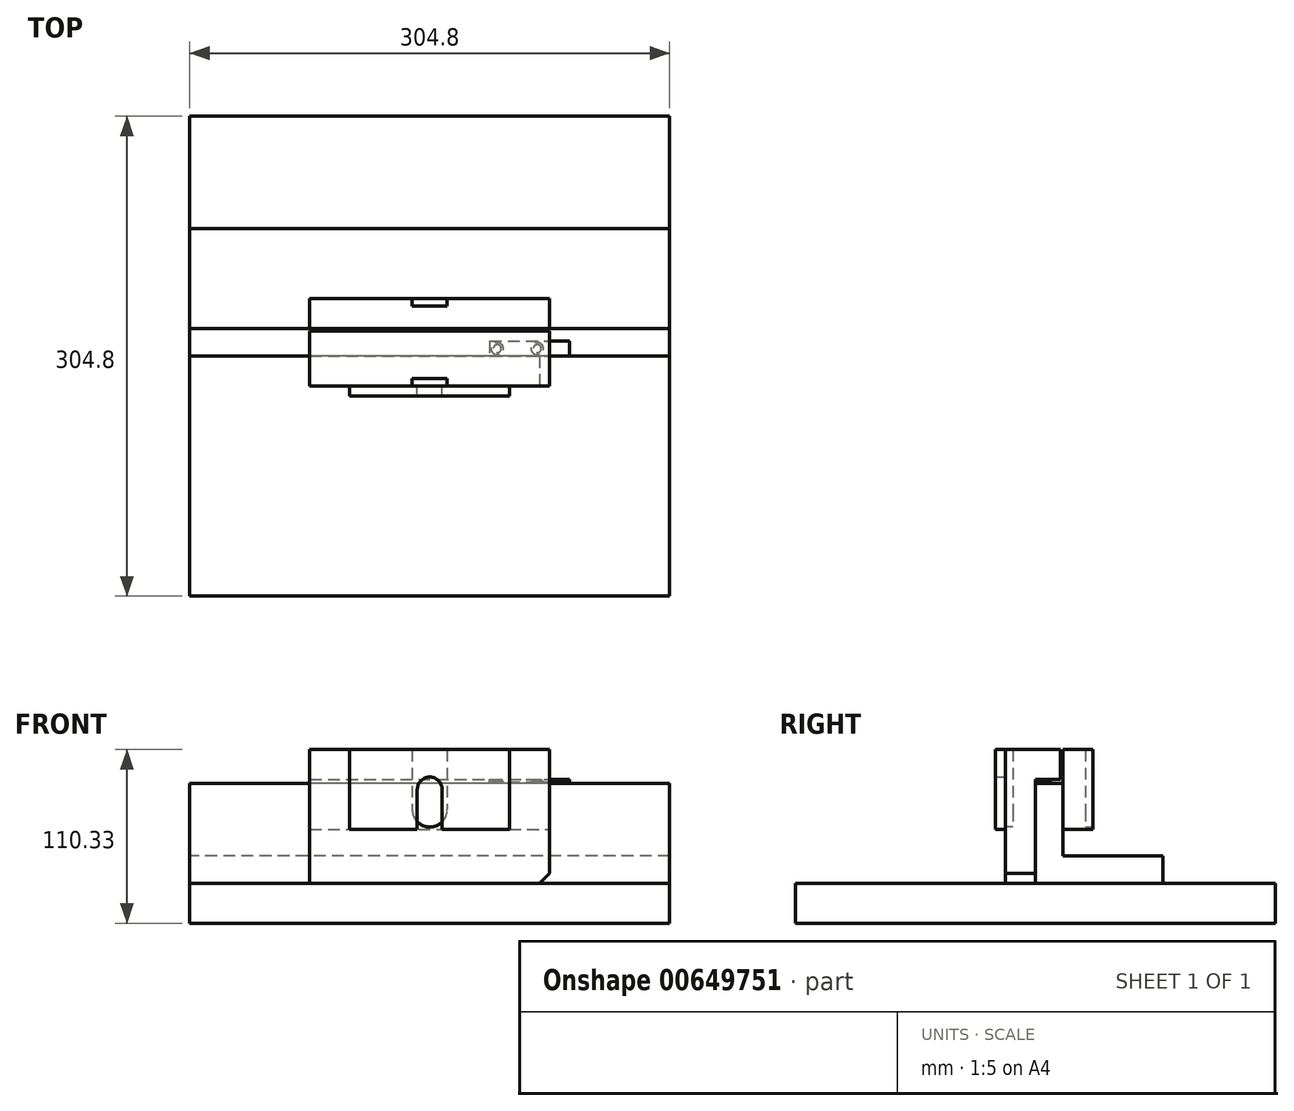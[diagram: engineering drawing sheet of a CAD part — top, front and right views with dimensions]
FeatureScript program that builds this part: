
annotation { "Feature Type Name" : "Feature", "Feature Type Description" : "" }
export const myFeature = defineFeature(function(context is Context, id is Id, definition is map)
    precondition{}
    {
        {
            var Q0;
            Q0=qCreatedBy(makeId("Right.planeOp"),FACE);
            var sketch = newSketch(context, id + "F0", { "sketchPlane" : qUnion([Q0])});
            skLineSegment(sketch, "E0", {"start": v(0, 0) * mm, "end": v(0, 63.5) * mm});
            skLineSegment(sketch, "E1", {"start": v(0, 63.5) * mm, "end": v(17.46, 63.5) * mm});
            skLineSegment(sketch, "E2", {"start": v(17.46, 63.5) * mm, "end": v(17.46, 17.46) * mm});
            skLineSegment(sketch, "E3", {"start": v(17.46, 17.46) * mm, "end": v(80.96, 17.46) * mm});
            skLineSegment(sketch, "E4", {"start": v(80.96, 17.46) * mm, "end": v(80.96, 0) * mm});
            skLineSegment(sketch, "E5", {"start": v(80.96, 0) * mm, "end": v(0, 0) * mm});
            skSolve(sketch);
        }
        {
            var Q0;
            Q0 = qSketchRegion(id + "F0", true);
            extrude(context, id + "F1", {"entities" : qUnion([Q0]), "depth" : 304.8 * mm, "offsetDistance" : 25.4 * mm, "symmetric" : true});
        }
        {
            var Q0;
            Q0=makeQuery(id+"F1.opExtrude","SWEPT_FACE",FACE,{"disambiguationData":[OSD([sQuery(id+"F0.wireOp",EDGE,"E5")])]});
            var sketch = newSketch(context, id + "F2", { "sketchPlane" : qUnion([Q0])});
            skLineSegment(sketch, "E6.0", {"start": v(152.4, -152.4) * mm, "end": v(152.4, 152.4) * mm});
            skLineSegment(sketch, "E6.1", {"start": v(-152.4, -152.4) * mm, "end": v(-152.4, 152.4) * mm});
            skLineSegment(sketch, "E7.0", {"start": v(152.4, 152.4) * mm, "end": v(-152.4, 152.4) * mm});
            skLineSegment(sketch, "E8.0", {"start": v(152.4, -152.4) * mm, "end": v(-152.4, -152.4) * mm});
            skPoint(sketch, "E9.orphan", {"position": v(-152.4, 0) * mm});
            skPoint(sketch, "E10.orphan", {"position": v(-152.4, -80.96) * mm});
            skPoint(sketch, "E11.orphan", {"position": v(152.4, 0) * mm});
            skPoint(sketch, "E12.orphan", {"position": v(152.4, -80.96) * mm});
            skSolve(sketch);
        }
        {
            var Q0;
            Q0 = qSketchRegion(id + "F2", true);
            extrude(context, id + "F3", {"entities" : qUnion([Q0]), "depth" : 25.4 * mm, "offsetDistance" : 25.4 * mm});
        }
        {
            var Q0;
            Q0=makeQuery(id+"F1.opExtrude","SWEPT_FACE",FACE,{"disambiguationData":[OSD([sQuery(id+"F0.wireOp",EDGE,"E0")])]});
            var sketch = newSketch(context, id + "F4", { "sketchPlane" : qUnion([Q0])});
            skLineSegment(sketch, "E13.bottom", {"start": v(-76.2, 0) * mm, "end": v(76.2, 0) * mm});
            skLineSegment(sketch, "E13.top", {"start": v(-76.2, 84.93) * mm, "end": v(76.2, 84.93) * mm});
            skLineSegment(sketch, "E13.left", {"start": v(-76.2, 0) * mm, "end": v(-76.2, 84.93) * mm});
            skLineSegment(sketch, "E13.right", {"start": v(76.2, 0) * mm, "end": v(76.2, 84.93) * mm});
            skLineSegment(sketch, "E14", {"start": v(0, 0) * mm, "end": v(0, 84.93) * mm, "construction": true});
            skSolve(sketch);
        }
        {
            var Q0;
            Q0 = qSketchRegion(id + "F4", true);
            extrude(context, id + "F5", {"entities" : qUnion([Q0]), "depth" : 19.05 * mm, "offsetDistance" : 25.4 * mm});
        }
        {
            var Q0;
            Q0=makeQuery(id+"F5.opExtrude","CAP_FACE",FACE,{"disambiguationData":[OSD([sQuery(id+"F4.wireOp",EDGE,"E13.bottom"),sQuery(id+"F4.wireOp",EDGE,"E13.top"),sQuery(id+"F4.wireOp",EDGE,"E13.left"),sQuery(id+"F4.wireOp",EDGE,"E13.right")])],"isStart":true});
            var sketch = newSketch(context, id + "F6", { "sketchPlane" : qUnion([Q0])});
            skLineSegment(sketch, "E15.0", {"start": v(-76.2, 65.88) * mm, "end": v(-76.2, 84.93) * mm});
            skLineSegment(sketch, "E15.1", {"start": v(76.2, 84.93) * mm, "end": v(-76.2, 84.93) * mm});
            skLineSegment(sketch, "E15.2", {"start": v(76.2, 65.88) * mm, "end": v(76.2, 84.93) * mm});
            skLineSegment(sketch, "E16.0", {"start": v(76.2, 65.88) * mm, "end": v(-76.2, 65.88) * mm});
            skPoint(sketch, "E17.orphan", {"position": v(-76.2, 0) * mm});
            skPoint(sketch, "E18.orphan", {"position": v(76.2, 0) * mm});
            skSolve(sketch);
        }
        {
            var Q0;
            Q0 = qSketchRegion(id + "F6", true);
            extrude(context, id + "F7", {"entities" : qUnion([Q0]), "operationType" : NewBodyOperationType.ADD, "depth" : 15.88 * mm, "offsetDistance" : 25.4 * mm});
        }
        {
            var Q0;
            Q0=makeQuery(id+"F1.opExtrude","SWEPT_FACE",FACE,{"disambiguationData":[OSD([sQuery(id+"F0.wireOp",EDGE,"E2")])]});
            var sketch = newSketch(context, id + "F8", { "sketchPlane" : qUnion([Q0])});
            skLineSegment(sketch, "E19.0", {"start": v(-76.2, 34.13) * mm, "end": v(-76.2, 84.93) * mm});
            skLineSegment(sketch, "E19.1", {"start": v(76.2, 84.93) * mm, "end": v(-76.2, 84.93) * mm});
            skLineSegment(sketch, "E19.2", {"start": v(76.2, 34.13) * mm, "end": v(76.2, 84.93) * mm});
            skLineSegment(sketch, "E20.0", {"start": v(76.2, 34.13) * mm, "end": v(-76.2, 34.13) * mm});
            skPoint(sketch, "E21.orphan", {"position": v(-76.2, 65.88) * mm});
            skPoint(sketch, "E22.orphan", {"position": v(76.2, 65.88) * mm});
            skSolve(sketch);
        }
        {
            var Q0;
            Q0 = qSketchRegion(id + "F8", true);
            extrude(context, id + "F9", {"entities" : qUnion([Q0]), "depth" : 19.05 * mm, "offsetDistance" : 25.4 * mm});
        }
        {
            var Q0;
            Q0=makeQuery(id+"F5.opExtrude","SWEPT_EDGE",EDGE,{"disambiguationData":[OSD([sQuery(id+"F0.wireOp",EDGE,"E0"),sQuery(id+"F0.wireOp",EDGE,"E5"),sQuery(id+"F4.wireOp",EDGE,"E13.bottom"),sQuery(id+"F4.wireOp",EDGE,"E13.right")])]});
            chamfer(context, id + "F10", {"entities" : qUnion([Q0]), "width" : 6.35 * mm, "tangentPropagation" : true});
        }
        {
            var Q0;
            Q0=makeQuery(id+"F7.opExtrude","SWEPT_FACE",FACE,{"disambiguationData":[OSD([sQuery(id+"F6.wireOp",EDGE,"E16.0")])]});
            var sketch = newSketch(context, id + "F11", { "sketchPlane" : qUnion([Q0])});
            skLineSegment(sketch, "E23.0", {"start": v(38.1, 0) * mm, "end": v(88.9, 0) * mm});
            skLineSegment(sketch, "E24.0", {"start": v(88.9, -9.52) * mm, "end": v(88.9, 0) * mm});
            skLineSegment(sketch, "E25.0", {"start": v(38.1, -9.52) * mm, "end": v(38.1, 0) * mm});
            skLineSegment(sketch, "E26.0", {"start": v(38.1, -9.52) * mm, "end": v(88.9, -9.52) * mm});
            skPoint(sketch, "E27.orphan", {"position": v(76.2, 0) * mm});
            skPoint(sketch, "E28.orphan", {"position": v(-76.2, 0) * mm});
            skSolve(sketch);
        }
        {
            var Q0;
            Q0 = qSketchRegion(id + "F11", true);
            extrude(context, id + "F12", {"entities" : qUnion([Q0]), "depth" : 1.59 * mm, "offsetDistance" : 25.4 * mm});
        }
        {
            var Q0;
            Q0=makeQuery(id+"F12.opExtrude","CAP_FACE",FACE,{"disambiguationData":[OSD([sQuery(id+"F11.wireOp",EDGE,"E23.0"),sQuery(id+"F11.wireOp",EDGE,"E24.0"),sQuery(id+"F11.wireOp",EDGE,"E25.0"),sQuery(id+"F11.wireOp",EDGE,"E26.0")])],"isStart":false});
            var sketch = newSketch(context, id + "F13", { "sketchPlane" : qUnion([Q0])});
            skPoint(sketch, "E29", {"position": v(42.86, -4.76) * mm});
            skPoint(sketch, "E30", {"position": v(68.26, -4.76) * mm});
            skSolve(sketch);
        }
        {
            var Q0;
            Q0=sQuery(id+"F13.wireOp",VERTEX,"E29");
            var Q1;
            Q1=sQuery(id+"F13.wireOp",VERTEX,"E30");
            var Q2;
            Q2=makeQuery(id+"F12.opExtrude","SWEPT_BODY",BODY,{"disambiguationData":[OSD([sQuery(id+"F11.wireOp",EDGE,"E23.0"),sQuery(id+"F11.wireOp",EDGE,"E24.0"),sQuery(id+"F11.wireOp",EDGE,"E25.0"),sQuery(id+"F11.wireOp",EDGE,"E26.0")])]});
            hole(context, id + "F14", {"style" : HoleStyle.C_SINK, "endStyle" : HoleEndStyle.THROUGH, "standardTappedOrClearance" : lookupTablePath({ "standard" : "ANSI", "fit" : "Normal (ASME)", "size" : "#6", "type" : "Clearance" }), "standardBlindInLast" : lookupTablePath({ "fit" : "Free", "standard" : "ANSI", "size" : "#6", "type" : "Clearance" }), "holeDiameter" : 3.8 * mm, "cSinkDiameter" : 7.8 * mm, "cSinkAngle" : 82 * degree, "majorDiameter" : 6.35 * mm, "isTappedThrough" : true, "tappedDepth" : 12.7 * mm, "tapClearance" : 3, "locations" : qUnion([Q0, Q1]), "scope" : qUnion([Q2])});
        }
        {
            var Q0;
            Q0=makeQuery(id+"F5.opExtrude","CAP_FACE",FACE,{"disambiguationData":[OSD([sQuery(id+"F4.wireOp",EDGE,"E13.bottom"),sQuery(id+"F4.wireOp",EDGE,"E13.top"),sQuery(id+"F4.wireOp",EDGE,"E13.left"),sQuery(id+"F4.wireOp",EDGE,"E13.right")])],"isStart":false});
            var sketch = newSketch(context, id + "F15", { "sketchPlane" : qUnion([Q0])});
            skLineSegment(sketch, "E31.bottom", {"start": v(-11.11, 84.93) * mm, "end": v(11.11, 84.93) * mm});
            skLineSegment(sketch, "E31.left", {"start": v(-11.11, 84.93) * mm, "end": v(-11.11, 46.83) * mm});
            skLineSegment(sketch, "E31.right", {"start": v(11.11, 84.93) * mm, "end": v(11.11, 46.83) * mm});
            skLineSegment(sketch, "E32", {"start": v(0, 0) * mm, "end": v(0, 84.93) * mm, "construction": true});
            skPoint(sketch, "E33.orphan", {"position": v(-76.2, 0) * mm});
            skPoint(sketch, "E34.orphan", {"position": v(69.85, 0) * mm});
            skLineSegment(sketch, "E35", {"start": v(-11.11, 46.83) * mm, "end": v(11.11, 46.83) * mm, "construction": true});
            skArc(sketch, "E36", {"start": v(-11.11, 46.83) * mm, "mid": v(0, 35.72) * mm, "end": v(11.11, 46.83) * mm});
            skSolve(sketch);
        }
        {
            var Q0;
            Q0 = qSketchRegion(id + "F15", true);
            extrude(context, id + "F16", {"entities" : qUnion([Q0]), "operationType" : NewBodyOperationType.REMOVE, "oppositeDirection" : true, "depth" : 4.76 * mm, "offsetDistance" : 25.4 * mm});
        }
        {
            var Q0;
            Q0=makeQuery(id+"F9.opExtrude","CAP_FACE",FACE,{"disambiguationData":[OSD([sQuery(id+"F8.wireOp",EDGE,"E19.0"),sQuery(id+"F8.wireOp",EDGE,"E19.1"),sQuery(id+"F8.wireOp",EDGE,"E19.2"),sQuery(id+"F8.wireOp",EDGE,"E20.0")])],"isStart":false});
            var sketch = newSketch(context, id + "F17", { "sketchPlane" : qUnion([Q0])});
            skLineSegment(sketch, "E37.0", {"start": v(11.11, 84.93) * mm, "end": v(-11.11, 84.93) * mm});
            skLineSegment(sketch, "E37.1", {"start": v(11.11, 84.93) * mm, "end": v(11.11, 46.83) * mm});
            skLineSegment(sketch, "E37.2", {"start": v(-11.11, 84.93) * mm, "end": v(-11.11, 46.83) * mm});
            skLineSegment(sketch, "E37.3", {"start": v(0, 0) * mm, "end": v(0, 84.93) * mm});
            skPoint(sketch, "E37.4", {"position": v(76.2, 0) * mm});
            skPoint(sketch, "E37.5", {"position": v(-69.85, 0) * mm});
            skLineSegment(sketch, "E37.6", {"start": v(11.11, 46.83) * mm, "end": v(-11.11, 46.83) * mm});
            skArc(sketch, "E37.7", {"start": v(11.11, 46.83) * mm, "mid": v(0, 35.72) * mm, "end": v(-11.11, 46.83) * mm});
            skSolve(sketch);
        }
        {
            var Q0;
            Q0 = qSketchRegion(id + "F17", true);
            extrude(context, id + "F18", {"entities" : qUnion([Q0]), "operationType" : NewBodyOperationType.REMOVE, "oppositeDirection" : true, "depth" : 4.76 * mm, "offsetDistance" : 25.4 * mm});
        }
        {
            var Q0;
            Q0=makeQuery(id+"F5.opExtrude","CAP_FACE",FACE,{"disambiguationData":[OSD([sQuery(id+"F4.wireOp",EDGE,"E13.bottom"),sQuery(id+"F4.wireOp",EDGE,"E13.top"),sQuery(id+"F4.wireOp",EDGE,"E13.left"),sQuery(id+"F4.wireOp",EDGE,"E13.right")])],"isStart":false});
            var sketch = newSketch(context, id + "F19", { "sketchPlane" : qUnion([Q0])});
            skLineSegment(sketch, "E38.bottom", {"start": v(50.8, 84.93) * mm, "end": v(-50.8, 84.93) * mm});
            skLineSegment(sketch, "E38.top", {"start": v(50.8, 34.13) * mm, "end": v(7.94, 34.13) * mm});
            skLineSegment(sketch, "E38.left", {"start": v(50.8, 84.93) * mm, "end": v(50.8, 34.13) * mm});
            skLineSegment(sketch, "E38.right", {"start": v(7.94, 59.53) * mm, "end": v(7.94, 34.13) * mm});
            skLineSegment(sketch, "E39", {"start": v(0, 46.83) * mm, "end": v(0, 59.53) * mm, "construction": true});
            skLineSegment(sketch, "E40.MirrorCS", {"start": v(-7.94, 59.53) * mm, "end": v(-7.94, 34.13) * mm});
            skLineSegment(sketch, "E41.MirrorCS", {"start": v(-50.8, 84.93) * mm, "end": v(-50.8, 34.13) * mm});
            skLineSegment(sketch, "E42.trimOffspring", {"start": v(-7.94, 34.13) * mm, "end": v(-50.8, 34.13) * mm});
            skArc(sketch, "E43", {"start": v(7.94, 59.53) * mm, "mid": v(0, 67.47) * mm, "end": v(-7.94, 59.53) * mm});
            skPoint(sketch, "E44.orphan", {"position": v(7.94, 84.93) * mm});
            skPoint(sketch, "E45.orphan", {"position": v(-7.94, 84.93) * mm});
            skSolve(sketch);
        }
        {
            var Q0;
            Q0 = qSketchRegion(id + "F19", true);
            extrude(context, id + "F20", {"entities" : qUnion([Q0]), "depth" : 6.35 * mm, "offsetDistance" : 25.4 * mm});
        }
    });
